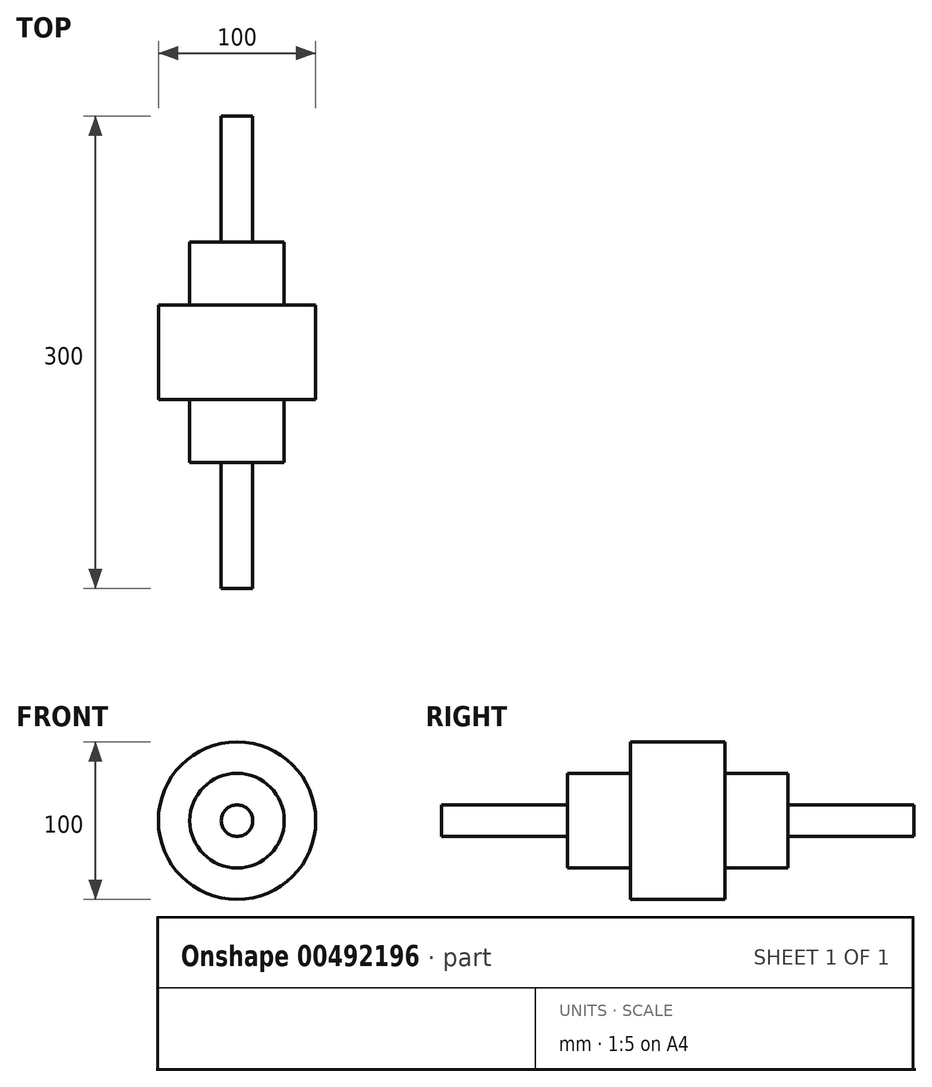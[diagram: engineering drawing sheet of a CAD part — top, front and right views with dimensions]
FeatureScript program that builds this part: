
annotation { "Feature Type Name" : "Feature", "Feature Type Description" : "" }
export const myFeature = defineFeature(function(context is Context, id is Id, definition is map)
    precondition{}
    {
        {
            var Q0;
            Q0=qCreatedBy(makeId("Front.planeOp"),FACE);
            var sketch = newSketch(context, id + "F0", { "sketchPlane" : qUnion([Q0])});
            skCircle(sketch, "E0", {"center": v(0, 0) * mm, "radius": 50 * mm});
            skSolve(sketch);
        }
        {
            var Q0;
            Q0 = qSketchRegion(id + "F0", true);
            extrude(context, id + "F1", {"entities" : qUnion([Q0]), "endBound" : BoundingType.SYMMETRIC, "depth" : (300 - (40 + 80) * 2) * mm, "offsetDistance" : 25 * mm});
        }
        {
            var Q0;
            Q0=makeQuery(id+"F1.opExtrude","CAP_FACE",FACE,{"disambiguationData":[OSD([sQuery(id+"F0.wireOp",EDGE,"E0")])],"isStart":false});
            var sketch = newSketch(context, id + "F2", { "sketchPlane" : qUnion([Q0])});
            skCircle(sketch, "E1", {"center": v(0, 0) * mm, "radius": 30 * mm});
            skSolve(sketch);
        }
        {
            var Q0;
            Q0 = qSketchRegion(id + "F2", true);
            extrude(context, id + "F3", {"entities" : qUnion([Q0]), "operationType" : NewBodyOperationType.ADD, "depth" : 40 * mm, "offsetDistance" : 25 * mm});
        }
        {
            var Q0;
            Q0=makeQuery(id+"F1.opExtrude","CAP_FACE",FACE,{"disambiguationData":[OSD([sQuery(id+"F0.wireOp",EDGE,"E0")])],"isStart":true});
            var sketch = newSketch(context, id + "F4", { "sketchPlane" : qUnion([Q0])});
            skCircle(sketch, "E2", {"center": v(0, 0) * mm, "radius": 30 * mm});
            skSolve(sketch);
        }
        {
            var Q0;
            Q0 = qSketchRegion(id + "F4", true);
            extrude(context, id + "F5", {"entities" : qUnion([Q0]), "operationType" : NewBodyOperationType.ADD, "depth" : 40 * mm, "offsetDistance" : 25 * mm});
        }
        {
            var Q0;
            Q0=makeQuery(id+"F5.opExtrude","CAP_FACE",FACE,{"disambiguationData":[OSD([sQuery(id+"F4.wireOp",EDGE,"E2")])],"isStart":false});
            var sketch = newSketch(context, id + "F6", { "sketchPlane" : qUnion([Q0])});
            skCircle(sketch, "E3", {"center": v(0, 0) * mm, "radius": 10 * mm});
            skSolve(sketch);
        }
        {
            var Q0;
            Q0 = qSketchRegion(id + "F6", true);
            extrude(context, id + "F7", {"entities" : qUnion([Q0]), "operationType" : NewBodyOperationType.ADD, "depth" : 80 * mm, "offsetDistance" : 25 * mm});
        }
        {
            var Q0;
            Q0=makeQuery(id+"F3.opExtrude","CAP_FACE",FACE,{"disambiguationData":[OSD([sQuery(id+"F2.wireOp",EDGE,"E1")])],"isStart":false});
            var sketch = newSketch(context, id + "F8", { "sketchPlane" : qUnion([Q0])});
            skCircle(sketch, "E4", {"center": v(0, 0) * mm, "radius": 10 * mm});
            skSolve(sketch);
        }
        {
            var Q0;
            Q0 = qSketchRegion(id + "F8", true);
            extrude(context, id + "F9", {"entities" : qUnion([Q0]), "operationType" : NewBodyOperationType.ADD, "depth" : 80 * mm, "offsetDistance" : 25 * mm});
        }
    });
